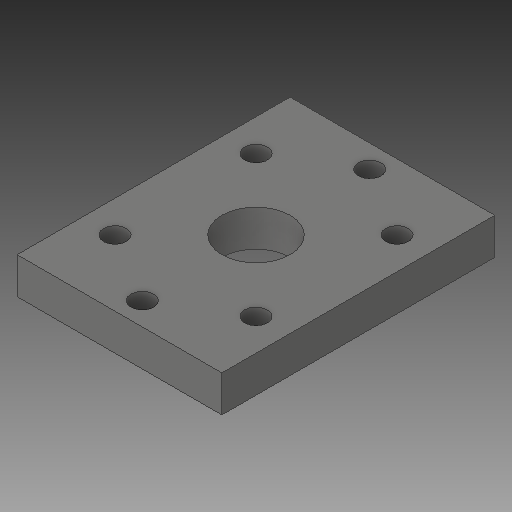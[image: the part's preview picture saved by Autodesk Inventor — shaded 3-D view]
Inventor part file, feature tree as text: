
AUTODESK INVENTOR PART (.ipt)
format: ipt  version: 2019 (Build 230136000, 136)  size: 121,856 bytes
history: native  units: mm
features: extrude x1, sketch x1
ambient origin geometry x8: Origin, YZ Plane, XZ Plane, XY Plane, X Axis, Y Axis, Z Axis, Center Point
bodies: Solid1 (feature_tree)
feature tree (2):
  extrude  "Extrusion1"  Depth=45.0mm
  sketch  "Sketch1"  dims[d6=60.0mm d7=45.0mm d8=31.0mm d9=5.0mm d10=5.0mm d11=5.0mm d12=5.0mm d13=5.0mm d14=5.0mm d15=15.0mm d16=8.0mm d17=0.0mm]
